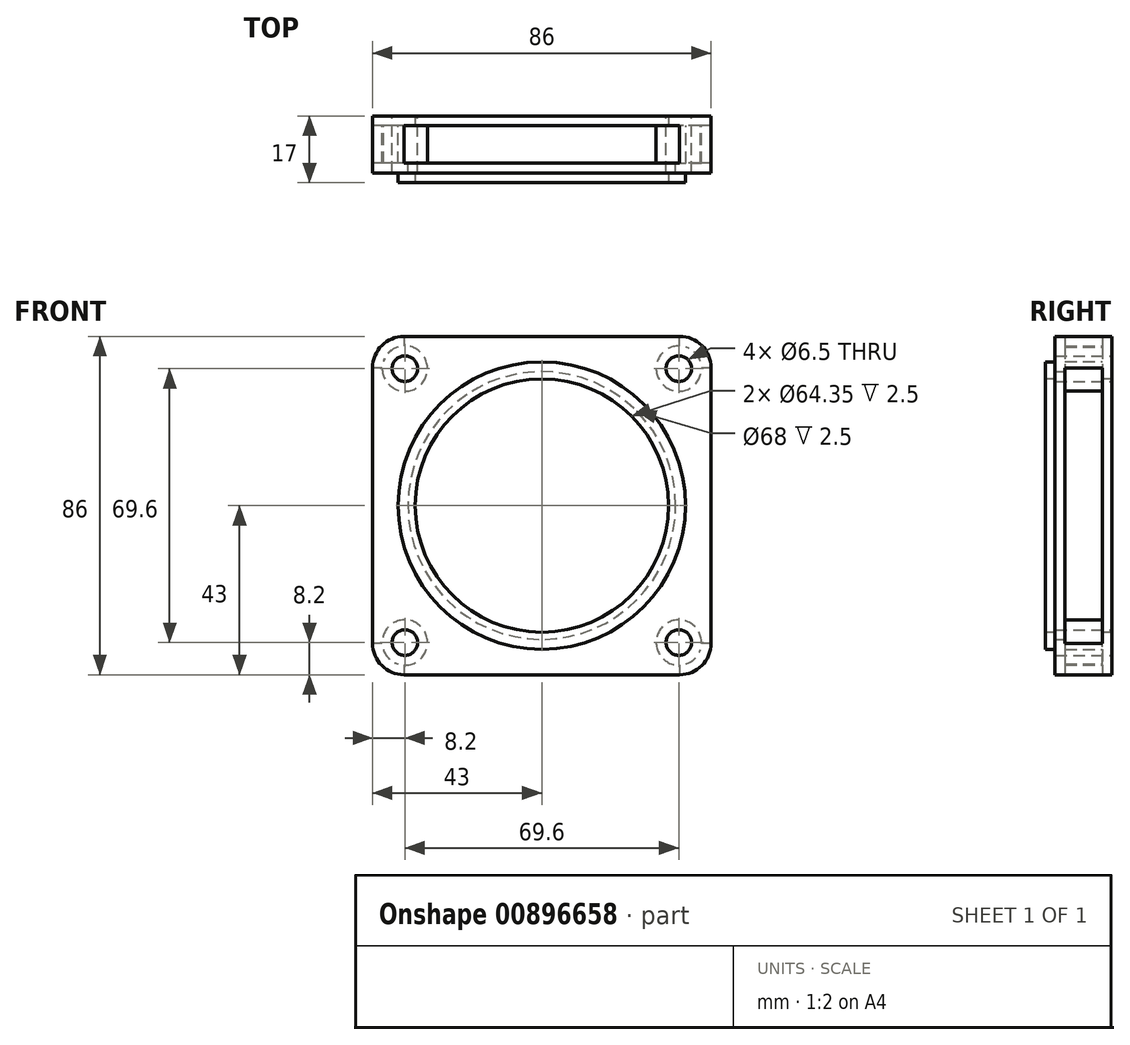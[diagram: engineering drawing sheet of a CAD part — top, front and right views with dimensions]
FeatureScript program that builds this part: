
annotation { "Feature Type Name" : "Feature", "Feature Type Description" : "" }
export const myFeature = defineFeature(function(context is Context, id is Id, definition is map)
    precondition{}
    {
        {
            var Q0;
            Q0=qCreatedBy(makeId("Front.planeOp"),FACE);
            var sketch = newSketch(context, id + "F0", { "sketchPlane" : qUnion([Q0])});
            skLineSegment(sketch, "E0.bottom", {"start": v(-43, 43) * mm, "end": v(43, 43) * mm});
            skLineSegment(sketch, "E0.top", {"start": v(-43, -43) * mm, "end": v(43, -43) * mm});
            skLineSegment(sketch, "E0.left", {"start": v(-43, 43) * mm, "end": v(-43, -43) * mm});
            skLineSegment(sketch, "E0.right", {"start": v(43, 43) * mm, "end": v(43, -43) * mm});
            skPoint(sketch, "E0.middle", {"position": v(0, 0) * mm});
            skCircle(sketch, "E1", {"center": v(0, 0) * mm, "radius": 36.5 * mm});
            skCircle(sketch, "E2", {"center": v(-34.8, 34.8) * mm, "radius": 3.25 * mm});
            skCircle(sketch, "E3", {"center": v(34.8, 34.8) * mm, "radius": 3.25 * mm});
            skCircle(sketch, "E4", {"center": v(-34.8, -34.8) * mm, "radius": 3.25 * mm});
            skCircle(sketch, "E5", {"center": v(34.8, -34.8) * mm, "radius": 3.25 * mm});
            skCircle(sketch, "E6", {"center": v(0, 0) * mm, "radius": 7 * mm});
            skSolve(sketch);
        }
        {
            var Q0;
            Q0=makeQuery(id+"F0.imprint","IMPRINT",FACE,{"disambiguationData":[TD([[makeQuery(id+"F0.imprint","IMPRINT",EDGE,{"derivedFrom":sQuery(id+"F0.wireOp",EDGE,"E1")}),1.0]])]});
            extrude(context, id + "F1", {"entities" : qUnion([Q0]), "depth" : 17 * mm, "offsetDistance" : 25 * mm});
        }
        {
            var Q0;
            Q0 = qSketchRegion(id + "F0", true);
            extrude(context, id + "F2", {"entities" : qUnion([Q0]), "operationType" : NewBodyOperationType.ADD, "depth" : 14.5 * mm, "offsetDistance" : 25 * mm});
        }
        {
            var Q0;
            Q0=makeQuery(id+"F2.opExtrude","SWEPT_EDGE",EDGE,{"disambiguationData":[OSD([sQuery(id+"F0.wireOp",EDGE,"E0.top"),sQuery(id+"F0.wireOp",EDGE,"E0.left")])]});
            var Q1;
            Q1=makeQuery(id+"F2.opExtrude","SWEPT_EDGE",EDGE,{"disambiguationData":[OSD([sQuery(id+"F0.wireOp",EDGE,"E0.top"),sQuery(id+"F0.wireOp",EDGE,"E0.right")])]});
            var Q2;
            Q2=makeQuery(id+"F2.opExtrude","SWEPT_EDGE",EDGE,{"disambiguationData":[OSD([sQuery(id+"F0.wireOp",EDGE,"E0.bottom"),sQuery(id+"F0.wireOp",EDGE,"E0.right")])]});
            var Q3;
            Q3=makeQuery(id+"F2.opExtrude","SWEPT_EDGE",EDGE,{"disambiguationData":[OSD([sQuery(id+"F0.wireOp",EDGE,"E0.bottom"),sQuery(id+"F0.wireOp",EDGE,"E0.left")])]});
            fillet(context, id + "F3", {"entities" : qUnion([Q0, Q1, Q2, Q3]), "radius" : 8 * mm, "tangentPropagation" : true, "allowEdgeOverflow" : false});
        }
        {
            var Q0;
            Q0=makeQuery(id+"F2.opExtrude","SWEPT_FACE",FACE,{"disambiguationData":[OSD([sQuery(id+"F0.wireOp",EDGE,"E0.right")])]});
            var Q1;
            Q1=makeQuery(id+"F2.opExtrude","SWEPT_FACE",FACE,{"disambiguationData":[OSD([sQuery(id+"F0.wireOp",EDGE,"E0.top")])]});
            var Q2;
            Q2=makeQuery(id+"F2.opExtrude","SWEPT_FACE",FACE,{"disambiguationData":[OSD([sQuery(id+"F0.wireOp",EDGE,"E0.left")])]});
            var Q3;
            Q3=makeQuery(id+"F2.opExtrude","SWEPT_FACE",FACE,{"disambiguationData":[OSD([sQuery(id+"F0.wireOp",EDGE,"E0.bottom")])]});
            shell(context, id + "F4", {"entities" : qUnion([Q0, Q1, Q2, Q3]), "thickness" : 2.5 * mm});
        }
        {
            var Q0;
            Q0=makeQuery(id+"F1.opExtrude","CAP_FACE",FACE,{"disambiguationData":[OSD([sQuery(id+"F0.wireOp",EDGE,"E1"),sQuery(id+"F0.wireOp",EDGE,"E6")])],"isStart":false});
            var sketch = newSketch(context, id + "F5", { "sketchPlane" : qUnion([Q0])});
            skCircle(sketch, "E7", {"center": v(0, 0) * mm, "radius": 32.18 * mm});
            skSolve(sketch);
        }
        {
            var Q0;
            Q0 = qSketchRegion(id + "F5", true);
            extrude(context, id + "F6", {"entities" : qUnion([Q0]), "operationType" : NewBodyOperationType.REMOVE, "oppositeDirection" : true, "depth" : 25 * mm, "offsetDistance" : 25 * mm});
        }
    });
